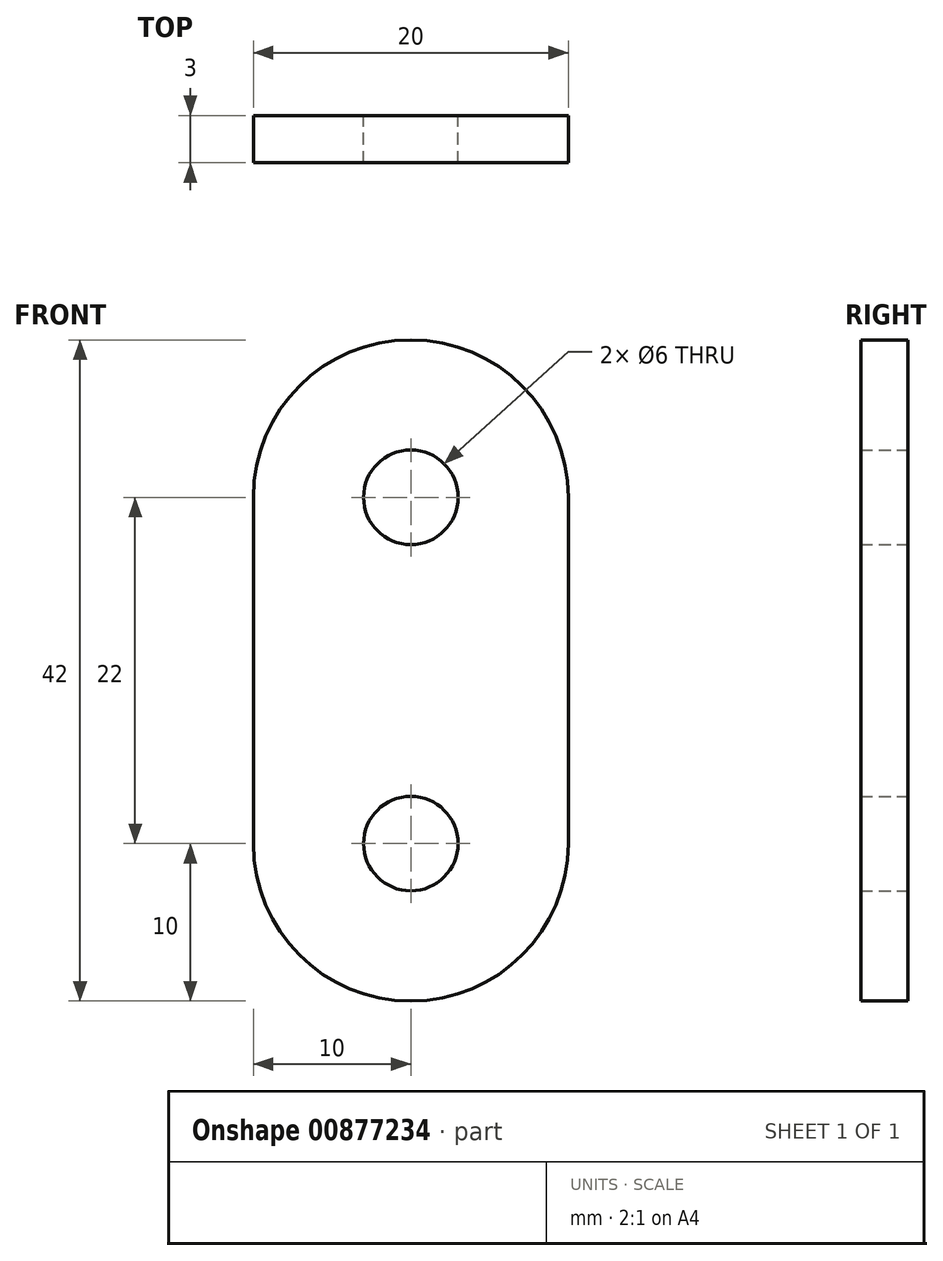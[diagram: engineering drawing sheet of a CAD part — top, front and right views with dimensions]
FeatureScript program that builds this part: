
annotation { "Feature Type Name" : "Feature", "Feature Type Description" : "" }
export const myFeature = defineFeature(function(context is Context, id is Id, definition is map)
    precondition{}
    {
        {
            var Q0;
            Q0=qCreatedBy(makeId("Front.planeOp"),FACE);
            var sketch = newSketch(context, id + "F0", { "sketchPlane" : qUnion([Q0])});
            skCircle(sketch, "E0", {"center": v(0, 11) * mm, "radius": 10 * mm});
            skLineSegment(sketch, "E1", {"start": v(-10, 11) * mm, "end": v(-10, 0) * mm});
            skLineSegment(sketch, "E2", {"start": v(-10, 0) * mm, "end": v(10, 0) * mm});
            skLineSegment(sketch, "E3", {"start": v(10, 0) * mm, "end": v(10, 11) * mm});
            skCircle(sketch, "E4", {"center": v(0, 11) * mm, "radius": 3 * mm});
            skSolve(sketch);
        }
        {
            var Q0;
            {var subQ0=sQuery(id+"F0.wireOp",EDGE,"E1");Q0=makeQuery(id+"F0.imprint","IMPRINT",FACE,{"disambiguationData":[TD([[makeQuery(id+"F0.imprint","IMPRINT",EDGE,{"derivedFrom":subQ0}),1.0]])]});}
            var Q1;
            Q1=makeQuery(id+"F0.imprint","IMPRINT",FACE,{"disambiguationData":[TD([[makeQuery(id+"F0.imprint","IMPRINT",EDGE,{"derivedFrom":sQuery(id+"F0.wireOp",EDGE,"E4")}),-1.0]])]});
            extrude(context, id + "F1", {"entities" : qUnion([Q0, Q1]), "depth" : 3 * mm, "offsetDistance" : 25 * mm});
        }
        {
            var Q0;
            Q0=makeQuery(id+"F1.opExtrude","SWEPT_BODY",BODY,{"disambiguationData":[OSD([sQuery(id+"F0.wireOp",EDGE,"E0"),sQuery(id+"F0.wireOp",EDGE,"E1"),sQuery(id+"F0.wireOp",EDGE,"E2"),sQuery(id+"F0.wireOp",EDGE,"E3"),sQuery(id+"F0.wireOp",EDGE,"E4")])]});
            var Q1;
            Q1=makeQuery(id+"F1.opExtrude","SWEPT_FACE",FACE,{"disambiguationData":[OSD([sQuery(id+"F0.wireOp",EDGE,"E2")])]});
            mirror(context, id + "F2", {"operationType" : NewBodyOperationType.ADD, "entities" : qUnion([Q0]), "mirrorPlane" : qUnion([Q1])});
        }
    });
